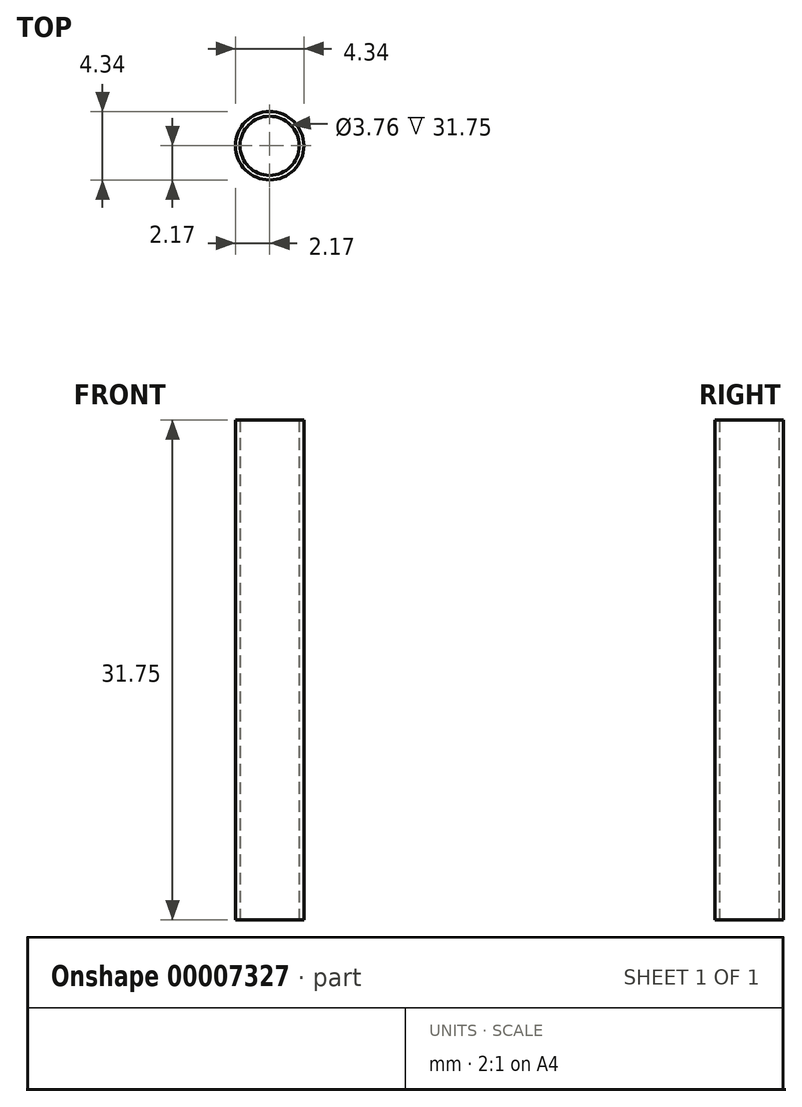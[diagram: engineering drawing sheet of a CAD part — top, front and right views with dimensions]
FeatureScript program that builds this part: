
annotation { "Feature Type Name" : "Feature", "Feature Type Description" : "" }
export const myFeature = defineFeature(function(context is Context, id is Id, definition is map)
    precondition{}
    {
        {
            var Q0;
            Q0=qCreatedBy(makeId("Front.planeOp"),FACE);
            var sketch = newSketch(context, id + "F0", { "sketchPlane" : qUnion([Q0])});
            skLineSegment(sketch, "E0.bottom", {"start": v(1.88, 0) * mm, "end": v(2.17, 0) * mm});
            skLineSegment(sketch, "E0.top", {"start": v(1.88, 31.75) * mm, "end": v(2.17, 31.75) * mm});
            skLineSegment(sketch, "E0.left", {"start": v(1.88, 0) * mm, "end": v(1.88, 31.75) * mm});
            skLineSegment(sketch, "E0.right", {"start": v(2.17, 0) * mm, "end": v(2.17, 31.75) * mm});
            skLineSegment(sketch, "E1", {"start": v(1.88, 0) * mm, "end": v(0, 0) * mm});
            skLineSegment(sketch, "E2", {"start": v(0, 0) * mm, "end": v(0, 31.75) * mm});
            skSolve(sketch);
        }
        {
            var Q0;
            Q0 = qSketchRegion(id + "F0", true);
            var Q1;
            Q1=sQuery(id+"F0.wireOp",EDGE,"E2");
            revolve(context, id + "F1", {"entities" : qUnion([Q0]), "axis" : qUnion([Q1]), "revolveType" : RevolveType.FULL});
        }
    });
